# Revit family: Herkules ER_Fugenprofile mit Sinuswelle Dehnfugenprofil Tagesfeldabschalung
name_source: partatom
category: Generic Models
units: mm (PartAtom-declared; Revit-internal decimal feet)

## family parameters
Always vertical = No
Can host rebar = No
Cut with Voids When Loaded = No
Part Type = Normal
Room Calculation Point = No
Round Connector Dimension = Use Diameter
Shared = No
Work Plane-Based = Yes

## types (3) — shared parameters
Abstand zum Rohr (h) = 90 mm  [stored 0.295276 ft]
Adresse = Iglauer Str. 6 86316 Friedberg
Basismaterial Herkules = Stahl S355 JR
Description = Schwerlastfugenprofil für industriell genutzte Betonbodenplatten
Höhe = 200 mm  [stored 0.656168 ft]
Keynote = Herkules ER
Lieferzeit = 2 weeks
Manufacturer = Guggemos GmbH
Telefon = +49 (0)8 21 / 455 969 0
Type Comments = HerkulesER_L2500
Type Image = Herkules ER.jpg
URL = https://www.fugenprofile.de
Unterstützt jumper_Height = 158 mm
Video = https://www.youtube.com
zero-valued in all types: Default Elevation

## per-type parameters (varying)
| type | Anzahl der Rohre | Anzahl der Stützen | Länge | Model | Startabstand zur Unterstützung |
| Herkules_ER_L2500_H200 | 5 | 3 | 2500 mm  [stored 8.2021 ft] | Schwerlastfugenprofil erschütterungsfrei überfah | 300 mm |
| Herkules_ER_L2000_L200 | 4 | 3 | 2000 mm  [stored 6.56168 ft] | Schwerlastfugenprofil erschütterungsfrei überfah | 500 mm  [stored 1.64042 ft] |
| Herkules_ER_L1500_H200 | 3 | 2 | 1500 mm  [stored 4.92126 ft] | Schwerlastfugenprofil erschütterungsfrei überfahrbar | 300 mm |

note: [stored X ft] marks values corroborated as IEEE doubles in the binary element streams (Revit-internal decimal feet)

## geometry (parser evidence)
native form markers: Sweep x16
no freeform markers — native parametric forms only
